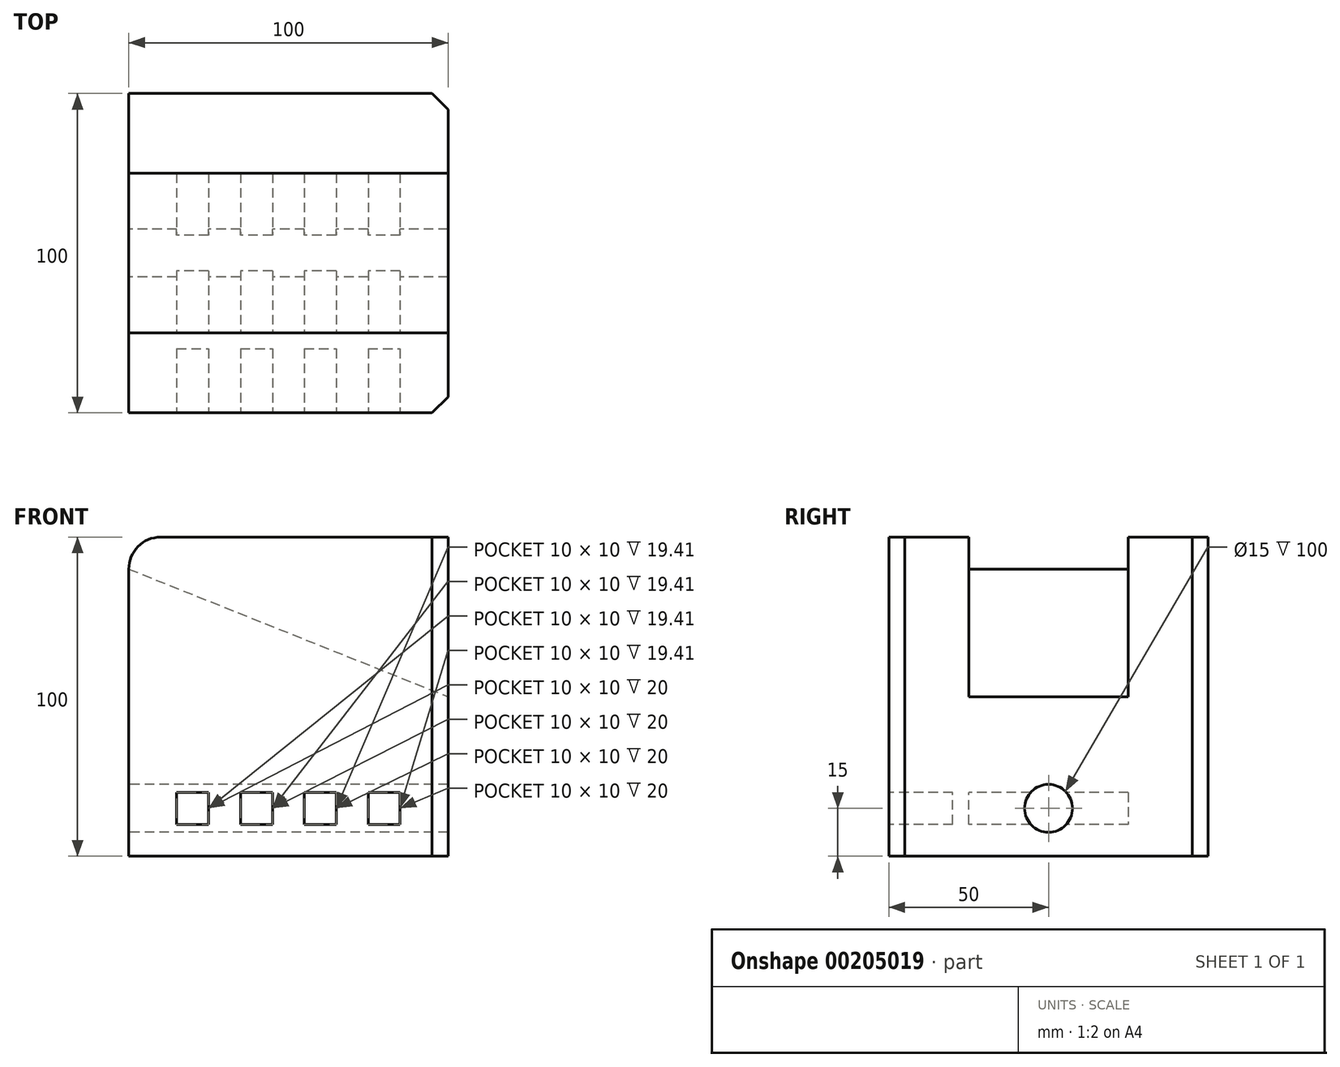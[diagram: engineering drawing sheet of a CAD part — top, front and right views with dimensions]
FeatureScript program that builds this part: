
annotation { "Feature Type Name" : "Feature", "Feature Type Description" : "" }
export const myFeature = defineFeature(function(context is Context, id is Id, definition is map)
    precondition{}
    {
        {
            var Q0;
            Q0=qCreatedBy(makeId("Front.planeOp"),FACE);
            var sketch = newSketch(context, id + "F0", { "sketchPlane" : qUnion([Q0])});
            skLineSegment(sketch, "E0", {"start": v(0, 90) * mm, "end": v(0, 0) * mm});
            skLineSegment(sketch, "E1", {"start": v(0, 0) * mm, "end": v(100, 0) * mm});
            skLineSegment(sketch, "E2", {"start": v(100, 0) * mm, "end": v(100, 50) * mm});
            skLineSegment(sketch, "E3", {"start": v(100, 50) * mm, "end": v(0, 90) * mm});
            skLineSegment(sketch, "E4", {"start": v(0, 0) * mm, "end": v(0, 10) * mm});
            skLineSegment(sketch, "E5", {"start": v(0, 10) * mm, "end": v(15, 10) * mm});
            skLineSegment(sketch, "E6.bottom", {"start": v(15, 10) * mm, "end": v(25, 10) * mm});
            skLineSegment(sketch, "E6.top", {"start": v(15, 20) * mm, "end": v(25, 20) * mm});
            skLineSegment(sketch, "E6.left", {"start": v(15, 10) * mm, "end": v(15, 20) * mm});
            skLineSegment(sketch, "E6.right", {"start": v(25, 10) * mm, "end": v(25, 20) * mm});
            skLineSegment(sketch, "E7", {"start": v(25, 10) * mm, "end": v(35, 10) * mm});
            skLineSegment(sketch, "E8.bottom", {"start": v(35, 10) * mm, "end": v(45, 10) * mm});
            skLineSegment(sketch, "E8.top", {"start": v(35, 20) * mm, "end": v(45, 20) * mm});
            skLineSegment(sketch, "E8.left", {"start": v(35, 10) * mm, "end": v(35, 20) * mm});
            skLineSegment(sketch, "E8.right", {"start": v(45, 10) * mm, "end": v(45, 20) * mm});
            skLineSegment(sketch, "E9", {"start": v(45, 10) * mm, "end": v(55, 10) * mm});
            skLineSegment(sketch, "E10.bottom", {"start": v(55, 10) * mm, "end": v(65, 10) * mm});
            skLineSegment(sketch, "E10.top", {"start": v(55, 20) * mm, "end": v(65, 20) * mm});
            skLineSegment(sketch, "E10.left", {"start": v(55, 10) * mm, "end": v(55, 20) * mm});
            skLineSegment(sketch, "E10.right", {"start": v(65, 10) * mm, "end": v(65, 20) * mm});
            skLineSegment(sketch, "E11", {"start": v(65, 10) * mm, "end": v(75, 10) * mm});
            skLineSegment(sketch, "E12.bottom", {"start": v(75, 10) * mm, "end": v(85, 10) * mm});
            skLineSegment(sketch, "E12.top", {"start": v(75, 20) * mm, "end": v(85, 20) * mm});
            skLineSegment(sketch, "E12.left", {"start": v(75, 10) * mm, "end": v(75, 20) * mm});
            skLineSegment(sketch, "E12.right", {"start": v(85, 10) * mm, "end": v(85, 20) * mm});
            skSolve(sketch);
        }
        {
            var Q0;
            Q0=makeQuery(id+"F0.imprint","IMPRINT",FACE,{"disambiguationData":[TD([[makeQuery(id+"F0.imprint","IMPRINT",EDGE,{"derivedFrom":sQuery(id+"F0.wireOp",EDGE,"E0")}),1.0]])]});
            extrude(context, id + "F1", {"entities" : qUnion([Q0]), "oppositeDirection" : true, "depth" : 100 * mm});
        }
        {
            var Q0;
            Q0=makeQuery(id+"F1.opExtrude","SWEPT_FACE",FACE,{"disambiguationData":[OSD([sQuery(id+"F0.wireOp",EDGE,"E1")])]});
            var sketch = newSketch(context, id + "F2", { "sketchPlane" : qUnion([Q0])});
            skLineSegment(sketch, "E13.bottom", {"start": v(0, 0) * mm, "end": v(100, 0) * mm});
            skLineSegment(sketch, "E13.top", {"start": v(0, -25) * mm, "end": v(100, -25) * mm});
            skLineSegment(sketch, "E13.left", {"start": v(0, 0) * mm, "end": v(0, -25) * mm});
            skLineSegment(sketch, "E13.right", {"start": v(100, 0) * mm, "end": v(100, -25) * mm});
            skLineSegment(sketch, "E14.bottom", {"start": v(100, -100) * mm, "end": v(0, -100) * mm});
            skLineSegment(sketch, "E14.top", {"start": v(100, -75) * mm, "end": v(0, -75) * mm});
            skLineSegment(sketch, "E14.left", {"start": v(100, -100) * mm, "end": v(100, -75) * mm});
            skLineSegment(sketch, "E14.right", {"start": v(0, -100) * mm, "end": v(0, -75) * mm});
            skSolve(sketch);
        }
        {
            var Q0;
            Q0=makeQuery(id+"F2.imprint","IMPRINT",FACE,{"disambiguationData":[TD([[makeQuery(id+"F2.imprint","IMPRINT",EDGE,{"derivedFrom":sQuery(id+"F2.wireOp",EDGE,"E13.bottom")}),-1.0]])]});
            var Q1;
            Q1=makeQuery(id+"F2.imprint","IMPRINT",FACE,{"disambiguationData":[TD([[makeQuery(id+"F2.imprint","IMPRINT",EDGE,{"derivedFrom":sQuery(id+"F2.wireOp",EDGE,"E14.bottom")}),1.0]])]});
            extrude(context, id + "F3", {"entities" : qUnion([Q0, Q1]), "operationType" : NewBodyOperationType.ADD, "oppositeDirection" : true, "depth" : 100 * mm});
        }
        {
            var Q0;
            Q0=makeQuery(id+"F3.opExtrude","CAP_EDGE",EDGE,{"disambiguationData":[OSD([sQuery(id+"F2.wireOp",EDGE,"E13.left")])],"isStart":false});
            var Q1;
            Q1=makeQuery(id+"F3.opExtrude","CAP_EDGE",EDGE,{"disambiguationData":[OSD([sQuery(id+"F2.wireOp",EDGE,"E14.right")])],"isStart":false});
            fillet(context, id + "F4", {"entities" : qUnion([Q0, Q1]), "radius" : 10 * mm, "tangentPropagation" : true, "allowEdgeOverflow" : false});
        }
        {
            var Q0;
            Q0=makeQuery(id+"F3.boolean.opBoolean","MERGE",FACE,{"derivedFrom":[makeQuery(id+"F1.opExtrude","SWEPT_FACE",FACE,{"disambiguationData":[OSD([sQuery(id+"F0.wireOp",EDGE,"E0")])]}),makeQuery(id+"F3.opExtrude","SWEPT_FACE",FACE,{"disambiguationData":[OSD([sQuery(id+"F2.wireOp",EDGE,"E13.left")])]}),makeQuery(id+"F3.opExtrude","SWEPT_FACE",FACE,{"disambiguationData":[OSD([sQuery(id+"F2.wireOp",EDGE,"E14.right")])]})]});
            var sketch = newSketch(context, id + "F5", { "sketchPlane" : qUnion([Q0])});
            skLineSegment(sketch, "E15", {"start": v(-50, 0) * mm, "end": v(-50, 15) * mm});
            skSolve(sketch);
        }
        {
            var Q0;
            Q0=sQuery(id+"F5.wireOp",VERTEX,"E15.end");
            var Q1;
            Q1=makeQuery(id+"F1.opExtrude","SWEPT_BODY",BODY,{"disambiguationData":[OSD([sQuery(id+"F0.wireOp",EDGE,"E0"),sQuery(id+"F0.wireOp",EDGE,"E1"),sQuery(id+"F0.wireOp",EDGE,"E2"),sQuery(id+"F0.wireOp",EDGE,"E3")])]});
            hole(context, id + "F6", {"style" : HoleStyle.SIMPLE, "endStyle" : HoleEndStyle.THROUGH, "holeDiameter" : 15 * mm, "locations" : qUnion([Q0]), "scope" : qUnion([Q1]), "isTappedThrough" : true});
        }
        {
            var Q0;
            Q0=makeQuery(id+"F0.imprint","IMPRINT",FACE,{"disambiguationData":[TD([[makeQuery(id+"F0.imprint","IMPRINT",EDGE,{"derivedFrom":sQuery(id+"F0.wireOp",EDGE,"E12.bottom")}),1.0]])]});
            var Q1;
            Q1=makeQuery(id+"F0.imprint","IMPRINT",FACE,{"disambiguationData":[TD([[makeQuery(id+"F0.imprint","IMPRINT",EDGE,{"derivedFrom":sQuery(id+"F0.wireOp",EDGE,"E10.bottom")}),1.0]])]});
            var Q2;
            Q2=makeQuery(id+"F0.imprint","IMPRINT",FACE,{"disambiguationData":[TD([[makeQuery(id+"F0.imprint","IMPRINT",EDGE,{"derivedFrom":sQuery(id+"F0.wireOp",EDGE,"E8.bottom")}),1.0]])]});
            var Q3;
            Q3=makeQuery(id+"F0.imprint","IMPRINT",FACE,{"disambiguationData":[TD([[makeQuery(id+"F0.imprint","IMPRINT",EDGE,{"derivedFrom":sQuery(id+"F0.wireOp",EDGE,"E6.bottom")}),1.0]])]});
            extrude(context, id + "F7", {"entities" : qUnion([Q0, Q1, Q2, Q3]), "operationType" : NewBodyOperationType.REMOVE, "oppositeDirection" : true, "depth" : 20 * mm});
        }
        {
            var Q0;
            Q0=makeQuery(id+"F3.boolean.opBoolean","MERGE",EDGE,{"derivedFrom":[makeQuery(id+"F1.opExtrude","CAP_EDGE",EDGE,{"disambiguationData":[OSD([sQuery(id+"F0.wireOp",EDGE,"E2")])],"isStart":true}),makeQuery(id+"F3.opExtrude","SWEPT_EDGE",EDGE,{"disambiguationData":[OSD([sQuery(id+"F2.wireOp",EDGE,"E13.bottom"),sQuery(id+"F2.wireOp",EDGE,"E13.right")])]})]});
            var Q1;
            Q1=makeQuery(id+"F3.boolean.opBoolean","MERGE",EDGE,{"derivedFrom":[makeQuery(id+"F1.opExtrude","CAP_EDGE",EDGE,{"disambiguationData":[OSD([sQuery(id+"F0.wireOp",EDGE,"E2")])],"isStart":false}),makeQuery(id+"F3.opExtrude","SWEPT_EDGE",EDGE,{"disambiguationData":[OSD([sQuery(id+"F2.wireOp",EDGE,"E14.bottom"),sQuery(id+"F2.wireOp",EDGE,"E14.left")])]})]});
            chamfer(context, id + "F8", {"entities" : qUnion([Q0, Q1]), "width" : 5 * mm, "tangentPropagation" : true});
        }
    });
